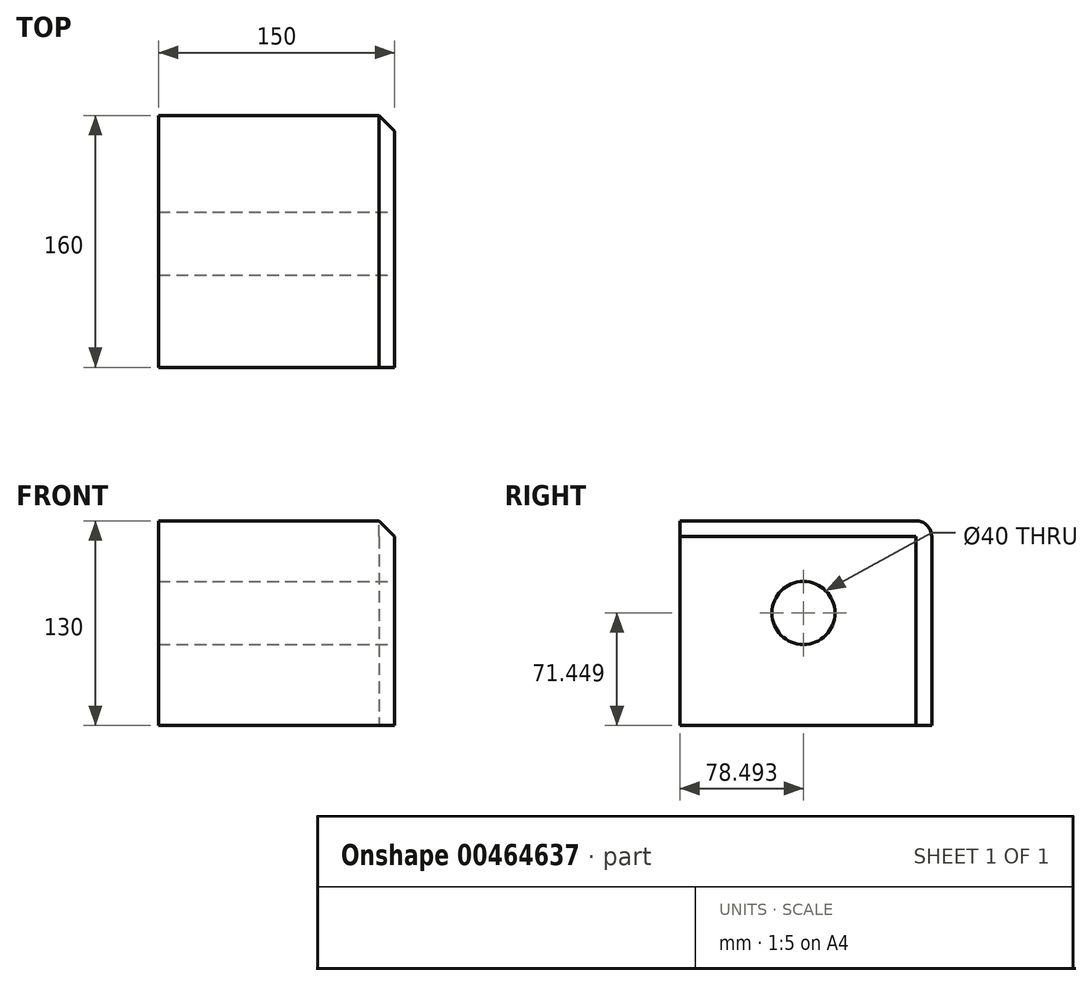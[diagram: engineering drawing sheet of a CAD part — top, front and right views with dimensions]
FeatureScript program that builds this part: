
annotation { "Feature Type Name" : "Feature", "Feature Type Description" : "" }
export const myFeature = defineFeature(function(context is Context, id is Id, definition is map)
    precondition{}
    {
        {
            var Q0;
            Q0=qCreatedBy(makeId("Right.planeOp"),FACE);
            var sketch = newSketch(context, id + "F0", { "sketchPlane" : qUnion([Q0])});
            skLineSegment(sketch, "E0.bottom", {"start": v(0, 0) * mm, "end": v(160, 0) * mm});
            skLineSegment(sketch, "E0.top", {"start": v(0, 130) * mm, "end": v(160, 130) * mm});
            skLineSegment(sketch, "E0.left", {"start": v(0, 0) * mm, "end": v(0, 130) * mm});
            skLineSegment(sketch, "E0.right", {"start": v(160, 0) * mm, "end": v(160, 130) * mm});
            skSolve(sketch);
        }
        {
            var Q0;
            Q0 = qSketchRegion(id + "F0", true);
            extrude(context, id + "F1", {"entities" : qUnion([Q0]), "depth" : 150 * mm});
        }
        {
            var Q0;
            Q0=makeQuery(id+"F1.opExtrude","SWEPT_EDGE",EDGE,{"disambiguationData":[OSD([sQuery(id+"F0.wireOp",EDGE,"E0.top"),sQuery(id+"F0.wireOp",EDGE,"E0.right")])]});
            fillet(context, id + "F2", {"entities" : qUnion([Q0]), "radius" : 10 * mm, "tangentPropagation" : true, "allowEdgeOverflow" : false});
        }
        {
            var Q0;
            Q0=makeQuery(id+"F1.opExtrude","CAP_EDGE",EDGE,{"disambiguationData":[OSD([sQuery(id+"F0.wireOp",EDGE,"E0.top")])],"isStart":false});
            var Q1;
            Q1=makeQuery(id+"F1.opExtrude","CAP_EDGE",EDGE,{"disambiguationData":[OSD([sQuery(id+"F0.wireOp",EDGE,"E0.right")])],"isStart":false});
            var Q2;
            {var subQ0=sQuery(id+"F0.wireOp",EDGE,"E0.right");var subQ1=sQuery(id+"F0.wireOp",EDGE,"E0.top");Q2=makeQuery(id+"F2.opFillet","BLEND_EDGE",EDGE,{"blendedFrom":[makeQuery(id+"F1.opExtrude","SWEPT_EDGE",EDGE,{"disambiguationData":[OSD([subQ1,subQ0])]}),makeQuery(id+"F1.opExtrude","CAP_FACE",FACE,{"disambiguationData":[OSD([sQuery(id+"F0.wireOp",EDGE,"E0.bottom"),subQ1,sQuery(id+"F0.wireOp",EDGE,"E0.left"),subQ0])],"isStart":false})],"blendedInto":[makeQuery(id+"F1.opExtrude","CAP_FACE",FACE,{"disambiguationData":[OSD([sQuery(id+"F0.wireOp",EDGE,"E0.bottom"),subQ1,sQuery(id+"F0.wireOp",EDGE,"E0.left"),subQ0])],"isStart":false})]});}
            chamfer(context, id + "F3", {"entities" : qUnion([Q0, Q1, Q2]), "width" : 10 * mm, "tangentPropagation" : true});
        }
        {
            var Q0;
            Q0=makeQuery(id+"F1.opExtrude","CAP_FACE",FACE,{"disambiguationData":[OSD([sQuery(id+"F0.wireOp",EDGE,"E0.bottom"),sQuery(id+"F0.wireOp",EDGE,"E0.top"),sQuery(id+"F0.wireOp",EDGE,"E0.left"),sQuery(id+"F0.wireOp",EDGE,"E0.right")])],"isStart":false});
            var sketch = newSketch(context, id + "F4", { "sketchPlane" : qUnion([Q0])});
            skCircle(sketch, "E1", {"center": v(78.5, 71.45) * mm, "radius": 20 * mm});
            skSolve(sketch);
        }
        {
            var Q0;
            Q0=makeQuery(id+"F4.imprint","IMPRINT",FACE,{"disambiguationData":[TD([[makeQuery(id+"F4.imprint","IMPRINT",EDGE,{"derivedFrom":sQuery(id+"F4.wireOp",EDGE,"E1")}),1.0]])]});
            extrude(context, id + "F5", {"entities" : qUnion([Q0]), "operationType" : NewBodyOperationType.REMOVE, "oppositeDirection" : true, "depth" : 265 * mm});
        }
    });
